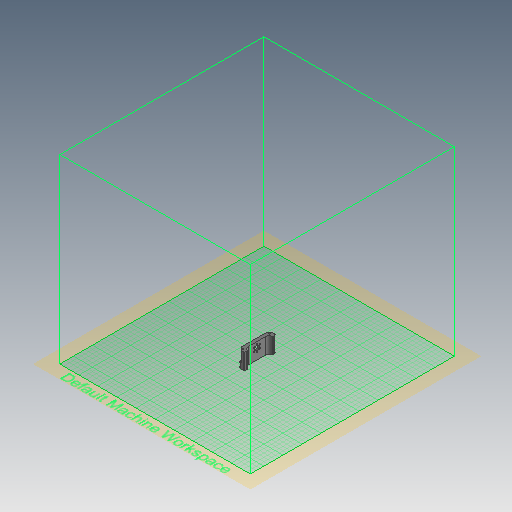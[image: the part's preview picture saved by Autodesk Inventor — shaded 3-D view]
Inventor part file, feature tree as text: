
AUTODESK INVENTOR PART (.ipt)
format: ipt  version: 2020 (Build 240168000, 168)  size: 636,928 bytes
history: native  units: mm
features: sketch x9, extrude x8, chamfer x3, projected_geometry x3, other x1, fillet x1
ambient origin geometry x8: Origin, YZ Plane, XZ Plane, XY Plane, X Axis, Y Axis, Z Axis, Center Point
bodies: Body1 (feature_tree)
feature tree (25):
  other  "Твердое тело1"
  extrude  "Выдавливание1"  Depth=35.0mm TaperAngle=0.0deg
  sketch  "Эскиз2"
  extrude  "Выдавливание4"  Depth=20.6mm
  extrude  "Выдавливание5"  Depth=15.0mm
  sketch  "Эскиз5"
  extrude  "Выдавливание8"  Depth=2.5mm
  extrude  "Выдавливание9"  Depth=60.0mm TaperAngle=360.0deg
  chamfer  "Фаска2"  Distance=11.0mm
  sketch  "Эскиз6"
  extrude  "Выдавливание10"  Depth=4.0mm
  fillet  "Сопряжение1"  Radius=4.0mm
  extrude  "Выдавливание11"  Depth=40.5mm TaperAngle=0.0deg
  extrude  "Выдавливание12"  Depth=4.0mm
  chamfer  "Фаска3"  Distance=4.0mm
  chamfer  "Фаска4"  Distance=3.5mm
  sketch  "Эскиз1"
  projected_geometry  "Спроецированная петля1"
  sketch  "Эскиз3"
  sketch  "Эскиз4"
  projected_geometry  "Спроецированная петля2"
  sketch  "Эскиз7"
  sketch  "Эскиз8"
  projected_geometry  "Спроецированная петля3"
  sketch  "Эскиз9"
